# Revit family: Domotics-DomesticRanges-GEWISS-CHORUS_POWER-SOCKET-OUTLET_ITADEU_RCBO
name_source: partatom
category: Apparecchi elettrici
revit_build: Autodesk Revit 2016 (Build: 20161004_0715(x64)
units: mm (PartAtom-declared; Revit-internal decimal feet)

## family parameters
Condiviso = Sì
Host = Superficie
Mantenere orientamento annotazione = Sì
Punto di calcolo locali = Sì
Quota connettore circolare = Usa diametro
Taglio con vuoti quando caricato = Sì
Tipo di parte = Normale

## types (3) — shared parameters
Breaking capacity = 3KA
Breaking capacity: = 1.25 In (100 position changes)
Catalogue = DOMOTICS
Catalogue Range = CHORUS - DOMESTIC RANGE
Category = Dual amperage interlocked socket-outlet
Corpo presa = <Per categoria>
Description. = Dual amperage interlocked socket-outlet
Description: = 2P+E - 16A
Electrocod = 0131
Fronte presa = Titanio
Glow Wire Test = 850°C
IDF = ae46ce6d-9601-4703-b9c2-fed7680ff1dc
IDT = e6612f92-24f5-4fa8-8dbd-28f08fe27080
Idn = 10MA
Insulation resistance = &gt; 5 MOhm
Miniature circuit breakers = 1P+N 16A
No. Chorus modules: = 4
Produttore = GEWISS S.p.A.
Prolonged operation (no.of position changes) = 10.000 at In 250 V ac cosÃ˜=0,8
Prospetto di default = 1219 mm
Protection = Miniature circuit breaker + residual current device
Resistance at test voltage = 2000 V at 50 Hz for 1 minute
SEO = Socket outlet
Socket-out type = P40
Standard: = English
Standard; = IEC 60884-1; EN 61009-1; EN 61008-1
Technical sheet = https://www.gewiss.com
Terminal grip on cable traction = &gt; 50 N
Terminal tightening capacity flexible cables (mm2) = min. 0,75 - max. 2x4
Terminal tightening capacity rigid cables (mm2) = min. 0,5 - max. 2x2,5
Thermo-pressure with ball = 125
Type: = Interlocked
URL = https://www.gewiss.com
Version file RFA = 19.0
Voltage: = 230V ac
Wiring terminals = With screw

## per-type parameters (varying)
| type | Colour | Descrizione | EAN code | Modello |
| GW12322 - INT SOC+R.M.C.BR. 4M 1P+N 16A P30/17/11B | Black | INT SOC+R.M.C.BR. 4M 1P+N 16A P30/17/11B | 8011564267350 | GW12322 |
| GW10322 - INT S.O. 4M 2P+E 16A P30/17-RCCB 1P+N  W | White | INT S.O. 4M 2P+E 16A P30/17-RCCB 1P+N  W | 8011564262492 | GW10322 |
| GW14322 - INT SOC+R.M.C.BR. 4M 1P+N 16A P30/17/11T | Titanium | INT SOC+R.M.C.BR. 4M 1P+N 16A P30/17/11T | 8011564266728 | GW14322 |

note: source unit labels omitted for Thermo-pressure with ball — the stored unit's dimension contradicts the parameter name (converter mislabeling)
